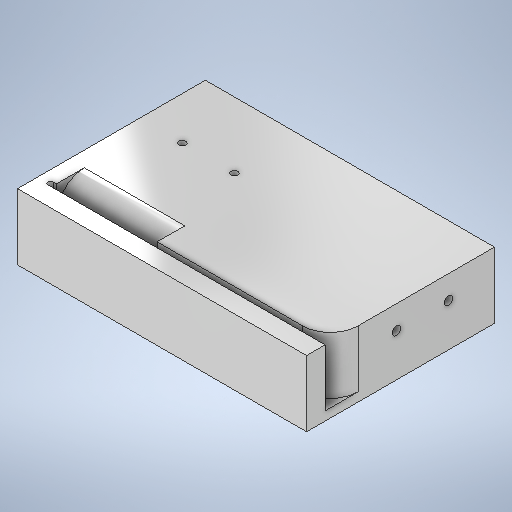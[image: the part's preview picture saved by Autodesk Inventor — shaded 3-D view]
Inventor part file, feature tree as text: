
AUTODESK INVENTOR PART (.ipt)
format: ipt  version: 2025 (Build 290162000, 162)  size: 410,624 bytes
history: native  units: in
note: dims shown in document units (in); Inventor stores cm internally (conversion verified against a paired STEP export)
features: sketch x11, extrude x6, hole x2
ambient origin geometry x8: Origin, YZ Plane, XZ Plane, XY Plane, X Axis, Y Axis, Z Axis, Center Point
bodies: Solid1 (feature_tree)
feature tree (19):
  extrude  "Extrusion1"  Depth=8.7402in
  extrude  "Extrusion7"  Depth=0.0591in
  hole  "Hole7"  [1 undecoded]
  sketch  "Sketch14"  dims[d176=2.0in d177=1.5748in d179=2.0in d180=0.3937in d182=0.3937in]
  extrude  "Extrusion8"  Depth=2.0in
  extrude  "Extrusion10"  Depth=0.3937in
  extrude  "Extrusion9"  Depth=0.6496in
  hole  "Hole8"  [1 undecoded]
  extrude  "Extrusion11"  Depth=0.3937in
  sketch  "Sketch12"  dims[d170=0.6496in d171=0.0in d173=0.4843in]
  sketch  "Sketch Rectangular Pattern3"  dims[d0=5.0in d1=8.7402in]
  sketch  "Sketch13"  dims[d174=0.5906in d175=1.0201in]
  sketch  "Sketch Rectangular Pattern4"  dims[d2=0.75in d3=0.0in d156=0.0591in]
  sketch  "Sketch Rectangular Pattern5"  dims[d157=0.5039in d159=0.0295in]
  sketch  "Sketch15"  dims[d184=0.0968in d185=0.2362in d186=0.248in d187=0.0787in d188=90.0deg d189=0.3465in d190=0.8108in]
  sketch  "Sketch Rectangular Pattern6"  dims[d160=3.1496in d161=2.0in]
  sketch  "Sketch16"  dims[d191=90.0deg]
  sketch  "Sketch Rectangular Pattern7"  dims[d162=0.2323in d163=1.5748in d165=2.0in d166=0.3937in d168=0.3937in]
  sketch  "Sketch17"  dims[d192=0.315in d193=0.315in d194=3.1102in d195=0.0in d196=1.5748in d198=2.0in d199=0.3937in d201=0.3937in d203=90.0deg d204=0.315in d205=1.5748in d207=2.0in d208=0.3937in d210=0.3937in d212=0.3937in d213=0.0in d214=1.9685in d215=0.0in d216=0.7992in d217=0.5906in d218=0.2362in d219=1.5748in d221=2.0in d222=0.3937in d224=0.3937in d226=0.0787in d227=0.2726in d228=0.1575in d229=0.0787in d230=90.0deg d231=0.315in d232=0.8108in d233=0.0in d234=0.0in d151=0.0394in d152=0.0394in d153=0.0394in d154=0.0059in d155=0.0098in d158=0.0295in]
note: 2 required parameter values undecoded (feature->parameter linkage not recoverable at this tier; creation-order binding heuristic only, values carry confidence <= 0.55)
